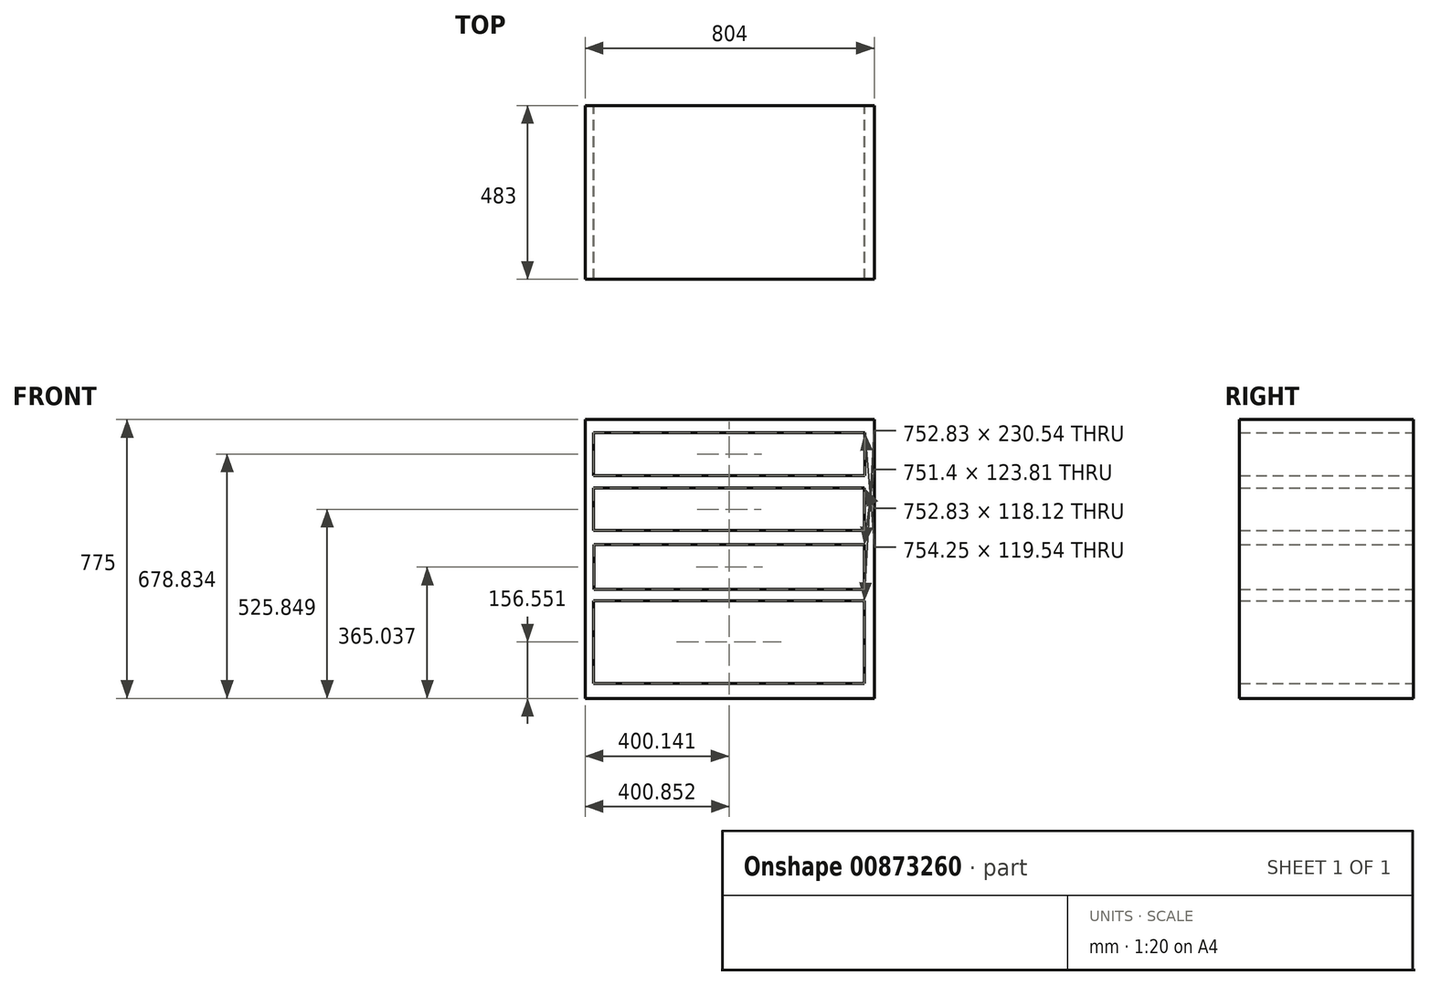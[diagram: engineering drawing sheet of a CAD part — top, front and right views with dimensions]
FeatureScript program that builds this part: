
annotation { "Feature Type Name" : "Feature", "Feature Type Description" : "" }
export const myFeature = defineFeature(function(context is Context, id is Id, definition is map)
    precondition{}
    {
        {
            var Q0;
            Q0=qCreatedBy(makeId("Front.planeOp"),FACE);
            var sketch = newSketch(context, id + "F0", { "sketchPlane" : qUnion([Q0])});
            skLineSegment(sketch, "E0.bottom", {"start": v(402, -387.5) * mm, "end": v(-402, -387.5) * mm});
            skLineSegment(sketch, "E0.top", {"start": v(402, 387.5) * mm, "end": v(-402, 387.5) * mm});
            skLineSegment(sketch, "E0.left", {"start": v(402, -387.5) * mm, "end": v(402, 387.5) * mm});
            skLineSegment(sketch, "E0.right", {"start": v(-402, -387.5) * mm, "end": v(-402, 387.5) * mm});
            skPoint(sketch, "E0.middle", {"position": v(0, 0) * mm});
            skLineSegment(sketch, "E1.bottom", {"start": v(-378.27, 351.1) * mm, "end": v(375.98, 351.1) * mm});
            skLineSegment(sketch, "E1.top", {"start": v(-378.27, 231.56) * mm, "end": v(375.98, 231.56) * mm});
            skLineSegment(sketch, "E1.left", {"start": v(-378.27, 351.1) * mm, "end": v(-378.27, 231.56) * mm});
            skLineSegment(sketch, "E1.right", {"start": v(375.98, 351.1) * mm, "end": v(375.98, 231.56) * mm});
            skLineSegment(sketch, "E2.bottom", {"start": v(-378.27, 197.4) * mm, "end": v(374.55, 197.4) * mm});
            skLineSegment(sketch, "E2.top", {"start": v(-378.27, 79.29) * mm, "end": v(374.55, 79.29) * mm});
            skLineSegment(sketch, "E2.left", {"start": v(-378.27, 197.4) * mm, "end": v(-378.27, 79.29) * mm});
            skLineSegment(sketch, "E2.right", {"start": v(374.55, 197.4) * mm, "end": v(374.55, 79.29) * mm});
            skLineSegment(sketch, "E3.bottom", {"start": v(-376.85, 39.44) * mm, "end": v(374.55, 39.44) * mm});
            skLineSegment(sketch, "E3.top", {"start": v(-376.85, -84.37) * mm, "end": v(374.55, -84.37) * mm});
            skLineSegment(sketch, "E3.left", {"start": v(-376.85, 39.44) * mm, "end": v(-376.85, -84.37) * mm});
            skLineSegment(sketch, "E3.right", {"start": v(374.55, 39.44) * mm, "end": v(374.55, -84.37) * mm});
            skLineSegment(sketch, "E4.bottom", {"start": v(-378.27, -115.68) * mm, "end": v(374.55, -115.68) * mm});
            skLineSegment(sketch, "E4.top", {"start": v(-378.27, -346.22) * mm, "end": v(374.55, -346.22) * mm});
            skLineSegment(sketch, "E4.left", {"start": v(-378.27, -115.68) * mm, "end": v(-378.27, -346.22) * mm});
            skLineSegment(sketch, "E4.right", {"start": v(374.55, -115.68) * mm, "end": v(374.55, -346.22) * mm});
            skSolve(sketch);
        }
        {
            var Q0;
            Q0 = qSketchRegion(id + "F0", true);
            extrude(context, id + "F1", {"entities" : qUnion([Q0]), "depth" : 483 * mm, "offsetDistance" : 25 * mm});
        }
    });
